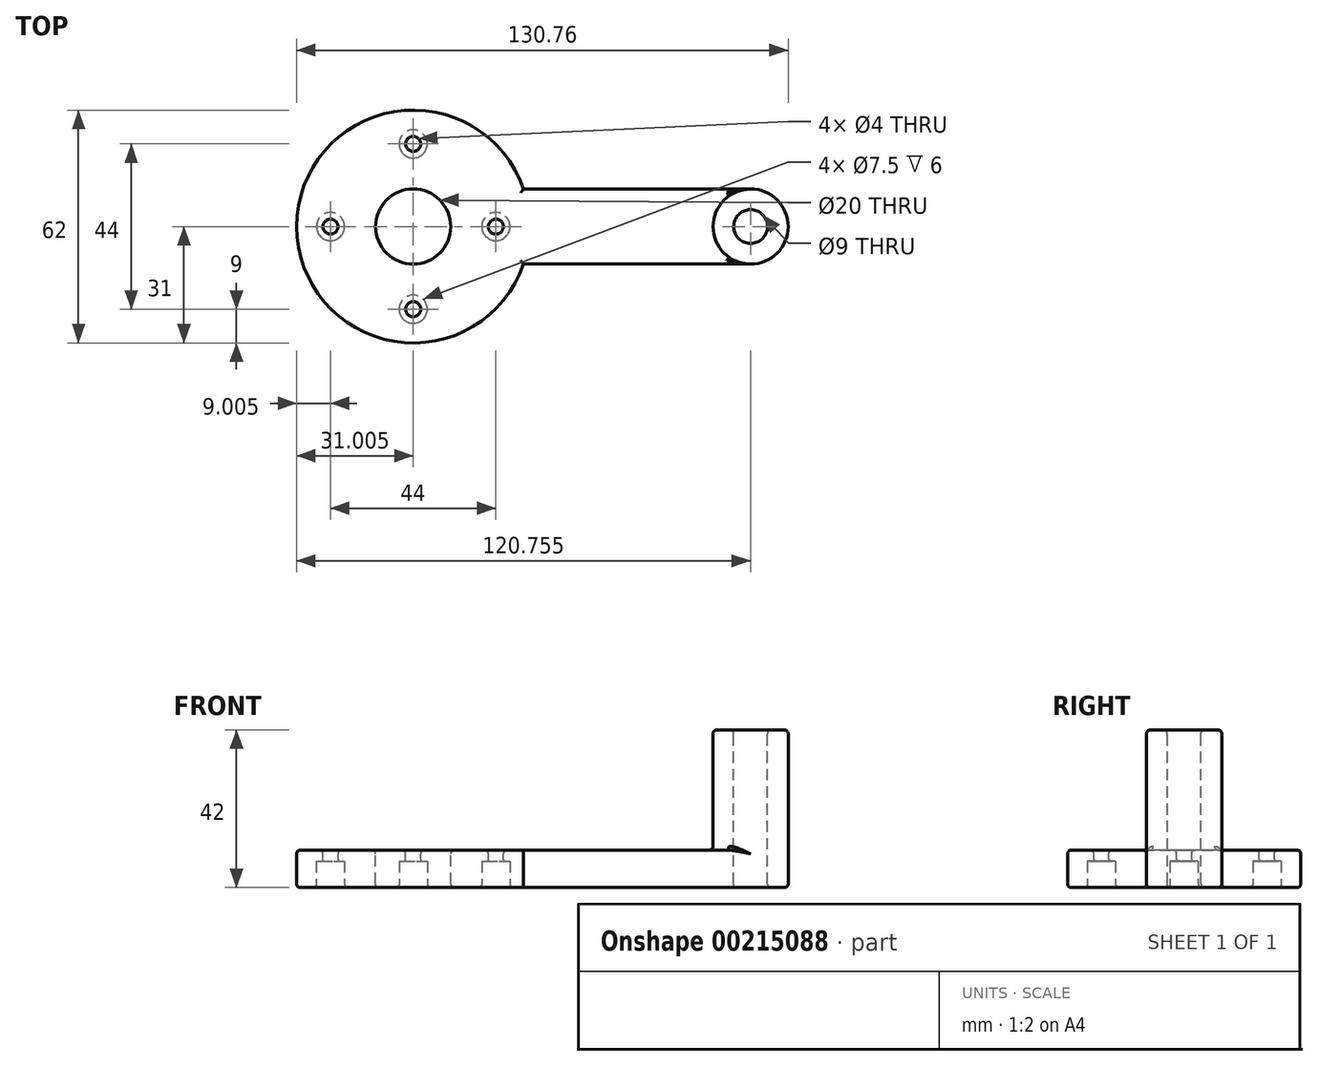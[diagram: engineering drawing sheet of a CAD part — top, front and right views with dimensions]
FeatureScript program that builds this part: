
annotation { "Feature Type Name" : "Feature", "Feature Type Description" : "" }
export const myFeature = defineFeature(function(context is Context, id is Id, definition is map)
    precondition{}
    {
        {
            var Q0;
            Q0=qCreatedBy(makeId("Top.planeOp"),FACE);
            var sketch = newSketch(context, id + "F0", { "sketchPlane" : qUnion([Q0])});
            skLineSegment(sketch, "E0", {"start": v(0, 0) * mm, "end": v(44.88, 0) * mm, "construction": true});
            skLineSegment(sketch, "E1", {"start": v(0, 0) * mm, "end": v(-44.88, 0) * mm, "construction": true});
            skCircle(sketch, "E2", {"center": v(-44.88, 0) * mm, "radius": 4.5 * mm});
            skCircle(sketch, "E3", {"center": v(44.88, 0) * mm, "radius": 4.5 * mm});
            skCircle(sketch, "E4", {"center": v(-44.88, 0) * mm, "radius": 10 * mm});
            skCircle(sketch, "E5", {"center": v(44.88, 0) * mm, "radius": 10 * mm});
            skLineSegment(sketch, "E6", {"start": v(-44.88, 10) * mm, "end": v(44.88, 10) * mm});
            skLineSegment(sketch, "E7", {"start": v(-44.88, -10) * mm, "end": v(44.88, -10) * mm});
            skCircle(sketch, "E8", {"center": v(-44.88, 0) * mm, "radius": 31 * mm});
            skCircle(sketch, "E9", {"center": v(-44.88, 0) * mm, "radius": 22 * mm, "construction": true});
            skPoint(sketch, "E10", {"position": v(-44.88, 22) * mm});
            skPoint(sketch, "E11", {"position": v(-66.87, 0) * mm});
            skPoint(sketch, "E12", {"position": v(-44.88, -22) * mm});
            skPoint(sketch, "E13", {"position": v(-22.88, 0) * mm});
            skCircle(sketch, "E14", {"center": v(-44.88, 22) * mm, "radius": 2 * mm});
            skCircle(sketch, "E15", {"center": v(-66.87, 0) * mm, "radius": 2 * mm});
            skCircle(sketch, "E16", {"center": v(-44.88, -22) * mm, "radius": 2 * mm});
            skCircle(sketch, "E17", {"center": v(-22.88, 0) * mm, "radius": 2 * mm});
            skSolve(sketch);
        }
        {
            var Q0;
            Q0=qSketchRegion(id+"F0",true);
            extrude(context, id + "F1", {"entities" : qUnion([Q0]), "oppositeDirection" : true, "depth" : 10 * mm});
        }
        {
            var Q0;
            Q0=makeQuery(id+"F0.imprint","IMPRINT",FACE,{"disambiguationData":[TD([[makeQuery(id+"F0.imprint","IMPRINT",EDGE,{"derivedFrom":sQuery(id+"F0.wireOp",EDGE,"E3")}),-1.0]])]});
            extrude(context, id + "F2", {"entities" : qUnion([Q0]), "operationType" : NewBodyOperationType.ADD, "depth" : 32 * mm});
        }
        {
            var Q0;
            Q0=makeQuery(id+"F1.opExtrude","CAP_FACE",FACE,{"disambiguationData":[OSD([sQuery(id+"F0.wireOp",EDGE,"E3"),sQuery(id+"F0.wireOp",EDGE,"E4"),sQuery(id+"F0.wireOp",EDGE,"E5"),sQuery(id+"F0.wireOp",EDGE,"E6"),sQuery(id+"F0.wireOp",EDGE,"E7"),sQuery(id+"F0.wireOp",EDGE,"E8"),sQuery(id+"F0.wireOp",EDGE,"E14"),sQuery(id+"F0.wireOp",EDGE,"E15"),sQuery(id+"F0.wireOp",EDGE,"E16"),sQuery(id+"F0.wireOp",EDGE,"E17")])],"isStart":false});
            var sketch = newSketch(context, id + "F3", { "sketchPlane" : qUnion([Q0])});
            skCircle(sketch, "E18", {"center": v(-44.88, 22) * mm, "radius": 3.75 * mm});
            skCircle(sketch, "E19", {"center": v(-22.88, 0) * mm, "radius": 3.75 * mm});
            skCircle(sketch, "E20", {"center": v(-44.88, -22) * mm, "radius": 3.75 * mm});
            skCircle(sketch, "E21", {"center": v(-66.87, 0) * mm, "radius": 3.75 * mm});
            skSolve(sketch);
        }
        {
            var Q0;
            Q0=qSketchRegion(id+"F3",true);
            extrude(context, id + "F4", {"entities" : qUnion([Q0]), "operationType" : NewBodyOperationType.REMOVE, "oppositeDirection" : true, "depth" : 7 * mm});
        }
        {
            var Q0;
            Q0=makeQuery(id+"F2.opExtrude","CAP_FACE",FACE,{"disambiguationData":[OSD([sQuery(id+"F0.wireOp",EDGE,"E2"),sQuery(id+"F0.wireOp",EDGE,"E4")])],"isStart":false});
            var Q1;
            Q1=makeQuery(id+"F1.opExtrude","CAP_FACE",FACE,{"disambiguationData":[OSD([sQuery(id+"F0.wireOp",EDGE,"E2"),sQuery(id+"F0.wireOp",EDGE,"E3"),sQuery(id+"F0.wireOp",EDGE,"E4"),sQuery(id+"F0.wireOp",EDGE,"E5"),sQuery(id+"F0.wireOp",EDGE,"E6"),sQuery(id+"F0.wireOp",EDGE,"E7")])],"isStart":true});
            var Q2;
            Q2=makeQuery(id+"F2.opExtrude","CAP_FACE",FACE,{"disambiguationData":[OSD([sQuery(id+"F0.wireOp",EDGE,"E3"),sQuery(id+"F0.wireOp",EDGE,"E5")])],"isStart":false});
            var Q3;
            Q3=makeQuery(id+"F1.opExtrude","CAP_FACE",FACE,{"disambiguationData":[OSD([sQuery(id+"F0.wireOp",EDGE,"E2"),sQuery(id+"F0.wireOp",EDGE,"E3"),sQuery(id+"F0.wireOp",EDGE,"E4"),sQuery(id+"F0.wireOp",EDGE,"E5"),sQuery(id+"F0.wireOp",EDGE,"E6"),sQuery(id+"F0.wireOp",EDGE,"E7")])],"isStart":false});
            fillet(context, id + "F5", {"entities" : qUnion([Q0, Q1, Q2, Q3]), "radius" : 1 * mm, "tangentPropagation" : true, "allowEdgeOverflow" : false});
        }
        {
            var Q0;
            Q0=makeQuery(id+"F1.opExtrude","SWEPT_FACE",FACE,{"disambiguationData":[OSD([sQuery(id+"F0.wireOp",EDGE,"E15")])]});
            var Q1;
            Q1=makeQuery(id+"F1.opExtrude","SWEPT_FACE",FACE,{"disambiguationData":[OSD([sQuery(id+"F0.wireOp",EDGE,"E16")])]});
            var Q2;
            Q2=makeQuery(id+"F1.opExtrude","SWEPT_FACE",FACE,{"disambiguationData":[OSD([sQuery(id+"F0.wireOp",EDGE,"E17")])]});
            var Q3;
            Q3=makeQuery(id+"F1.opExtrude","SWEPT_FACE",FACE,{"disambiguationData":[OSD([sQuery(id+"F0.wireOp",EDGE,"E14")])]});
            fillet(context, id + "F6", {"entities" : qUnion([Q0, Q1, Q2, Q3]), "radius" : .5 * mm, "tangentPropagation" : true, "allowEdgeOverflow" : false});
        }
    });
